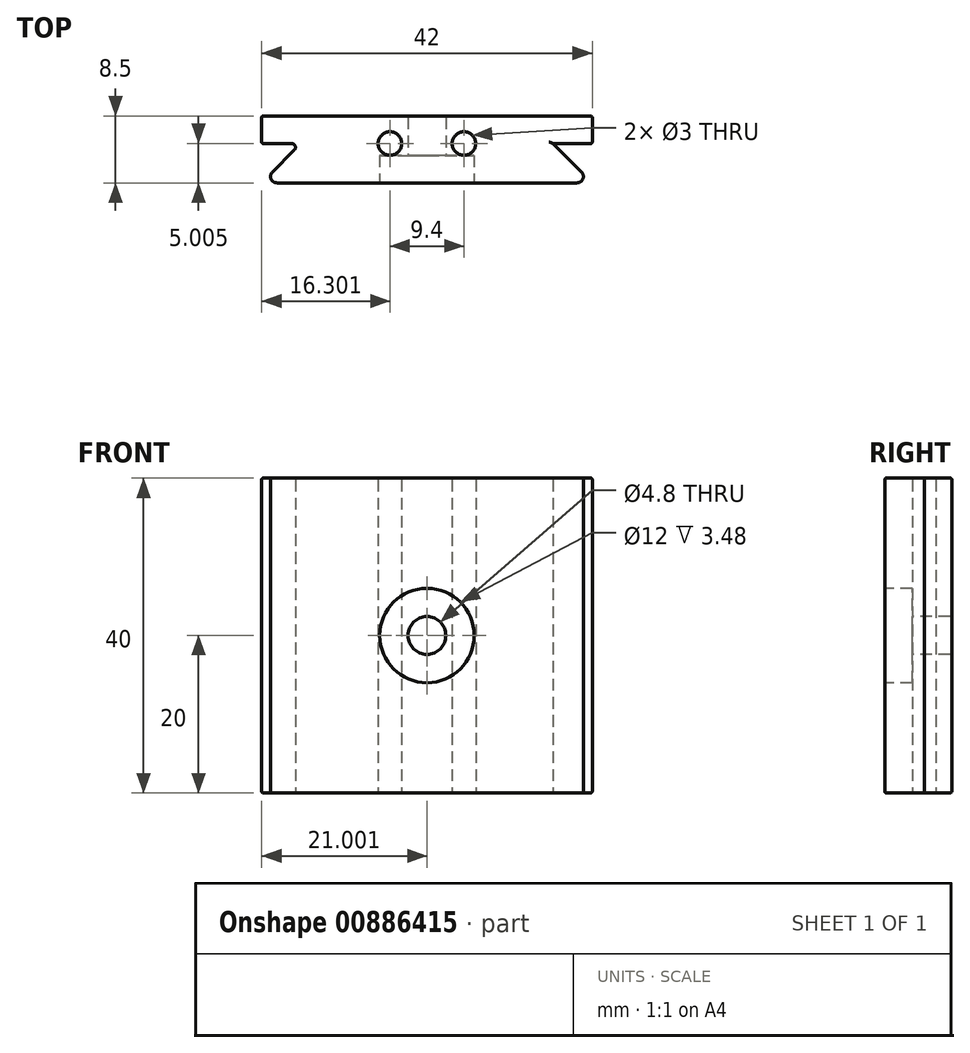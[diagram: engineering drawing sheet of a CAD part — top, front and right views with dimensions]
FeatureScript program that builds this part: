
annotation { "Feature Type Name" : "Feature", "Feature Type Description" : "" }
export const myFeature = defineFeature(function(context is Context, id is Id, definition is map)
    precondition{}
    {
        {
            var Q0;
            Q0=qCreatedBy(makeId("Top.planeOp"),FACE);
            var sketch = newSketch(context, id + "F0", { "sketchPlane" : qUnion([Q0])});
            skLineSegment(sketch, "E0.bottom", {"start": v(-21.16, 2.7) * mm, "end": v(-0.16, 2.7) * mm});
            skLineSegment(sketch, "E0.top", {"start": v(-21.16, -5.3) * mm, "end": v(-0.16, -5.3) * mm});
            skLineSegment(sketch, "E0.left", {"start": v(-21.16, 2.7) * mm, "end": v(-21.16, -0.3) * mm});
            skLineSegment(sketch, "E1", {"start": v(-21.16, 2.7) * mm, "end": v(-13.16, 2.7) * mm});
            skLineSegment(sketch, "E2", {"start": v(-16.16, -0.3) * mm, "end": v(-21.16, -5.3) * mm});
            skPoint(sketch, "E3.startSnap0", {"position": v(-0.16, 2.7) * mm});
            skLineSegment(sketch, "E4.trimOffspring", {"start": v(-16.16, -0.3) * mm, "end": v(-21.16, -0.3) * mm});
            skLineSegment(sketch, "E5", {"start": v(-0.16, 13.7) * mm, "end": v(-0.16, 2.7) * mm});
            skLineSegment(sketch, "E6.MirrorCS", {"start": v(20.84, 2.7) * mm, "end": v(12.84, 2.7) * mm});
            skLineSegment(sketch, "E7.MirrorCS", {"start": v(20.84, -5.3) * mm, "end": v(-0.16, -5.3) * mm});
            skLineSegment(sketch, "E8.MirrorCS", {"start": v(15.84, -0.3) * mm, "end": v(20.84, -5.3) * mm});
            skLineSegment(sketch, "E9.MirrorCS", {"start": v(15.84, -0.3) * mm, "end": v(20.84, -0.3) * mm});
            skLineSegment(sketch, "E10.MirrorCS", {"start": v(20.84, 2.7) * mm, "end": v(-0.16, 2.7) * mm});
            skLineSegment(sketch, "E11.MirrorCS", {"start": v(20.84, 2.7) * mm, "end": v(20.84, -0.3) * mm});
            skLineSegment(sketch, "E12", {"start": v(-0.16, -5.3) * mm, "end": v(-0.16, -1.8) * mm});
            skLineSegment(sketch, "E13", {"start": v(-0.16, -1.8) * mm, "end": v(4.54, -1.8) * mm});
            skLineSegment(sketch, "E14", {"start": v(4.54, -1.8) * mm, "end": v(4.54, -0.3) * mm});
            skCircle(sketch, "E15", {"center": v(4.54, -0.3) * mm, "radius": 1.5 * mm});
            skCircle(sketch, "E16.MirrorC", {"center": v(-4.86, -0.3) * mm, "radius": 1.5 * mm});
            skSolve(sketch);
        }
        {
            var Q0;
            Q0=makeQuery(id+"F0.imprint","IMPRINT",FACE,{"disambiguationData":[TD([[makeQuery(id+"F0.imprint","IMPRINT",EDGE,{"derivedFrom":sQuery(id+"F0.wireOp",EDGE,"E0.bottom")}),-1.0]])]});
            var Q1;
            {var subQ0=sQuery(id+"F0.wireOp",EDGE,"E7.MirrorCS");Q1=makeQuery(id+"F0.imprint","IMPRINT",FACE,{"disambiguationData":[TD([[makeQuery(id+"F0.imprint","IMPRINT",EDGE,{"derivedFrom":subQ0}),-1.0]])]});}
            extrude(context, id + "F1", {"entities" : qUnion([Q0, Q1]), "depth" : 40 * mm, "offsetDistance" : 25 * mm});
        }
        {
            var Q0;
            Q0=makeQuery(id+"F1.opExtrude","SWEPT_FACE",FACE,{"disambiguationData":[OSD([sQuery(id+"F0.wireOp",EDGE,"E0.top")])]});
            var sketch = newSketch(context, id + "F2", { "sketchPlane" : qUnion([Q0])});
            skCircle(sketch, "E17", {"center": v(-0.16, 20) * mm, "radius": 2.4 * mm});
            skCircle(sketch, "E18", {"center": v(-0.16, 20) * mm, "radius": 6 * mm});
            skPoint(sketch, "E19.trimOffspring.end.orphan", {"position": v(-21.16, 40) * mm});
            skPoint(sketch, "E20.orphan", {"position": v(-21.16, 0) * mm});
            skSolve(sketch);
        }
        {
            var Q0;
            Q0=makeQuery(id+"F2.imprint","IMPRINT",FACE,{"disambiguationData":[TD([[makeQuery(id+"F2.imprint","IMPRINT",EDGE,{"derivedFrom":sQuery(id+"F2.wireOp",EDGE,"E17")}),1.0]])]});
            extrude(context, id + "F3", {"entities" : qUnion([Q0]), "operationType" : NewBodyOperationType.REMOVE, "endBound" : BoundingType.THROUGH_ALL, "oppositeDirection" : true, "depth" : 25 * mm, "offsetDistance" : 25 * mm});
        }
        {
            var Q0;
            Q0=makeQuery(id+"F2.imprint","IMPRINT",FACE,{"disambiguationData":[TD([[makeQuery(id+"F2.imprint","IMPRINT",EDGE,{"derivedFrom":sQuery(id+"F2.wireOp",EDGE,"E17")}),-1.0]])]});
            extrude(context, id + "F4", {"entities" : qUnion([Q0]), "operationType" : NewBodyOperationType.REMOVE, "oppositeDirection" : true, "depth" : 3.48 * mm, "offsetDistance" : 25 * mm});
        }
        {
            var Q0;
            Q0=makeQuery(id+"F1.opExtrude","SWEPT_FACE",FACE,{"disambiguationData":[OSD([sQuery(id+"F0.wireOp",EDGE,"E0.bottom"),sQuery(id+"F0.wireOp",EDGE,"E1")])]});
            extrude(context, id + "F5", {"entities" : qUnion([Q0]), "operationType" : NewBodyOperationType.ADD, "depth" : 0.5 * mm, "offsetDistance" : 25 * mm});
        }
        {
            var Q0;
            Q0=makeQuery(id+"F1.opExtrude","SWEPT_EDGE",EDGE,{"disambiguationData":[OSD([sQuery(id+"F0.wireOp",EDGE,"E7.MirrorCS"),sQuery(id+"F0.wireOp",EDGE,"E8.MirrorCS")])]});
            var Q1;
            Q1=makeQuery(id+"F1.opExtrude","SWEPT_EDGE",EDGE,{"disambiguationData":[OSD([sQuery(id+"F0.wireOp",EDGE,"E0.top"),sQuery(id+"F0.wireOp",EDGE,"E2")])]});
            fillet(context, id + "F6", {"entities" : qUnion([Q0, Q1]), "radius" : .8 * mm, "tangentPropagation" : true, "allowEdgeOverflow" : false});
        }
        {
            var Q0;
            Q0=makeQuery(id+"F1.opExtrude","SWEPT_EDGE",EDGE,{"disambiguationData":[OSD([sQuery(id+"F0.wireOp",EDGE,"742e73fc-6181-445c-977f-03f215e344080.MirrorCS"),sQuery(id+"F0.wireOp",EDGE,"86195fd9-6974-4633-b4cc-74acbb69c7a60.MirrorCS")])]});
            var Q1;
            Q1=makeQuery(id+"F1.opExtrude","SWEPT_EDGE",EDGE,{"disambiguationData":[OSD([sQuery(id+"F0.wireOp",EDGE,"E2"),sQuery(id+"F0.wireOp",EDGE,"E4.trimOffspring")])]});
            fillet(context, id + "F7", {"entities" : qUnion([Q0, Q1]), "radius" : 0.5 * mm, "tangentPropagation" : true, "allowEdgeOverflow" : false});
        }
        {
            var Q0;
            {var subQ0=sQuery(id+"F0.wireOp",EDGE,"E1");var subQ1=sQuery(id+"F0.wireOp",EDGE,"E0.bottom");Q0=makeQuery(id+"F5.boolean.opBoolean","MERGE",FACE,{"derivedFrom":[makeQuery(id+"F1.opExtrude","CAP_FACE",FACE,{"disambiguationData":[OSD([subQ1,sQuery(id+"F0.wireOp",EDGE,"E0.top"),sQuery(id+"F0.wireOp",EDGE,"E0.left"),subQ0,sQuery(id+"F0.wireOp",EDGE,"E2"),sQuery(id+"F0.wireOp",EDGE,"6yD1ApCj-qosd-sSsQ-ZRap-KMrhpjR1ixWp"),sQuery(id+"F0.wireOp",EDGE,"E4.trimOffspring"),sQuery(id+"F0.wireOp",EDGE,"742e73fc-6181-445c-977f-03f215e344080.MirrorCS"),sQuery(id+"F0.wireOp",EDGE,"86195fd9-6974-4633-b4cc-74acbb69c7a60.MirrorCS")])],"isStart":false}),makeQuery(id+"F5.opExtrude","SWEPT_FACE",FACE,{"disambiguationData":[OSD([subQ1,subQ0]),TDD([makeQuery(id+"F1.opExtrude","CAP_EDGE",EDGE,{"disambiguationData":[OSD([subQ1,subQ0])],"isStart":false})])]})]});}
            var Q1;
            {var subQ0=sQuery(id+"F0.wireOp",EDGE,"E1");var subQ1=sQuery(id+"F0.wireOp",EDGE,"E0.bottom");Q1=makeQuery(id+"F5.boolean.opBoolean","MERGE",FACE,{"derivedFrom":[makeQuery(id+"F1.opExtrude","CAP_FACE",FACE,{"disambiguationData":[OSD([subQ1,sQuery(id+"F0.wireOp",EDGE,"E0.top"),sQuery(id+"F0.wireOp",EDGE,"E0.left"),subQ0,sQuery(id+"F0.wireOp",EDGE,"E2"),sQuery(id+"F0.wireOp",EDGE,"6yD1ApCj-qosd-sSsQ-ZRap-KMrhpjR1ixWp"),sQuery(id+"F0.wireOp",EDGE,"E4.trimOffspring"),sQuery(id+"F0.wireOp",EDGE,"742e73fc-6181-445c-977f-03f215e344080.MirrorCS"),sQuery(id+"F0.wireOp",EDGE,"86195fd9-6974-4633-b4cc-74acbb69c7a60.MirrorCS")])],"isStart":true}),makeQuery(id+"F5.opExtrude","SWEPT_FACE",FACE,{"disambiguationData":[OSD([subQ1,subQ0]),TDD([makeQuery(id+"F1.opExtrude","CAP_EDGE",EDGE,{"disambiguationData":[OSD([subQ1,subQ0])],"isStart":true})])]})]});}
            var Q2;
            Q2=makeQuery(id+"F5.opExtrude","CAP_FACE",FACE,{"disambiguationData":[OSD([sQuery(id+"F0.wireOp",EDGE,"E0.bottom"),sQuery(id+"F0.wireOp",EDGE,"E1")])],"isStart":false});
            var Q3;
            Q3=makeQuery(id+"F4.boolean.opBoolean","COPY",EDGE,{"derivedFrom":makeQuery(id+"F4.opExtrude","CAP_EDGE",EDGE,{"disambiguationData":[OSD([sQuery(id+"F2.wireOp",EDGE,"E18")])],"isStart":true})});
            var Q4;
            Q4=makeQuery(id+"F1.opExtrude","SWEPT_EDGE",EDGE,{"disambiguationData":[OSD([sQuery(id+"F0.wireOp",EDGE,"E0.left"),sQuery(id+"F0.wireOp",EDGE,"E4.trimOffspring")])]});
            var Q5;
            Q5=makeQuery(id+"F1.opExtrude","SWEPT_EDGE",EDGE,{"disambiguationData":[OSD([sQuery(id+"F0.wireOp",EDGE,"E9.MirrorCS"),sQuery(id+"F0.wireOp",EDGE,"E11.MirrorCS")])]});
            fillet(context, id + "F8", {"entities" : qUnion([Q0, Q1, Q2, Q3, Q4, Q5]), "radius" : .2 * mm, "tangentPropagation" : true, "allowEdgeOverflow" : false});
        }
    });
